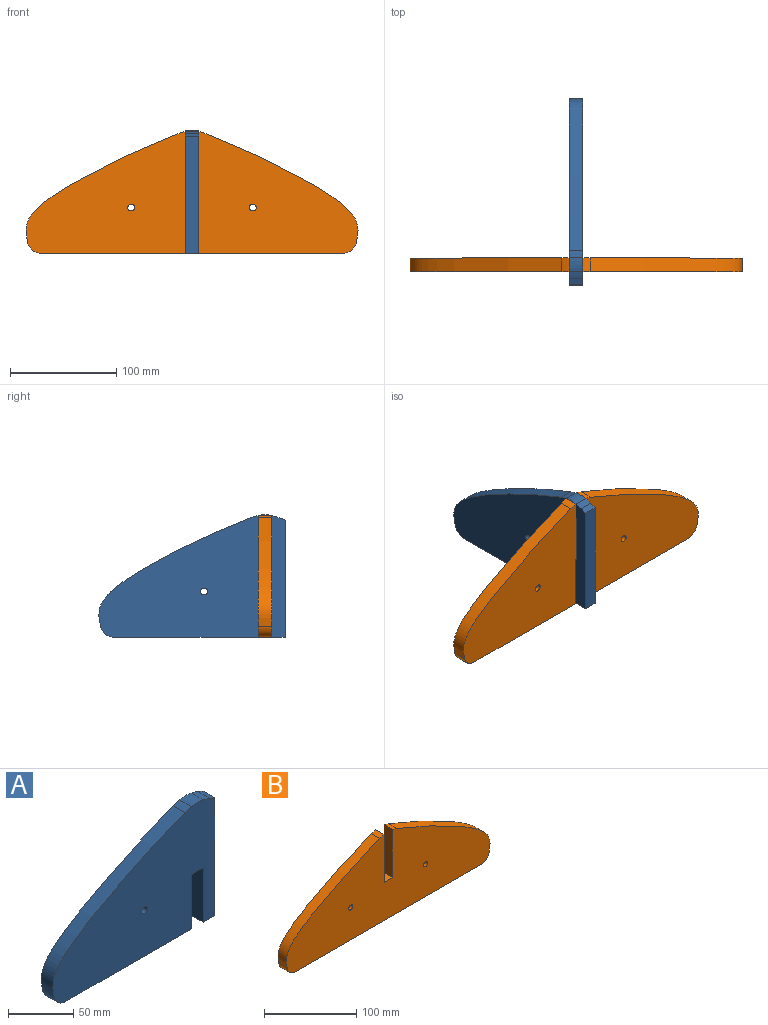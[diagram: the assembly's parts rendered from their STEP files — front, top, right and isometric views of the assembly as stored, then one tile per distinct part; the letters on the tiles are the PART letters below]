
ASSEMBLY  parts=2 mates=1
PART A: 15 faces, bbox 178.9x12.7x115.2 mm
  f0: extruded ~142.72x102mm, area 2355.1mm2, adj f1,f12,f13,f14
  f1: cylinder r=12.7mm len=12.7mm, axis (0,1,0), area 222.9mm2, adj f0,f2,f13,f14
  f2: plane 135.65x12.7mm, normal (0,0,-1), area 1722.8mm2, adj f1,f3,f13,f14
  f3: plane 50.8x12.7mm, normal (1,0,0), area 645.2mm2, adj f2,f4,f13,f14
  f4: plane 12.7x12.63mm, normal (0,0,-1), area 160.4mm2, adj f3,f5,f13,f14
  f5: plane 50.8x12.7mm, normal (-1,0,0), area 645.2mm2, adj f4,f6,f13,f14
  f6: plane 12.7x12.7mm, normal (0,0,-1), area 161.3mm2, adj f5,f7,f13,f14
  f7: plane 110.07x12.7mm, normal (1,0,0), area 1397.9mm2, adj f6,f8,f13,f14
  f8: extruded ~12.7x5.72mm, area 78mm2, adj f7,f9,f13,f14
  f9: cylinder r=50.8mm len=12.7mm, axis (0,1,0), area 91.9mm2, adj f8,f10,f13,f14
  f10: cylinder r=28.26mm len=12.7mm, axis (0,1,0), area 162.7mm2, adj f9,f12,f13,f14
  f11: cylinder r=3.17mm len=12.7mm, axis (0,1,0), area 253.4mm2, adj f13,f14
  f12: cylinder r=50.8mm len=12.7mm, axis (0,1,0), area 91.9mm2, adj f0,f10,f13,f14
  f13: plane 178.95x115.16mm, normal (0,-1,0), area 14079.7mm2, adj f0,f1,f2,f3,f4,f5,f6,f7
  f14: plane 178.95x115.16mm, normal (0,1,0), area 14079.7mm2, adj f0,f1,f2,f3,f4,f5,f6,f7
PART B: 14 faces, bbox 319.9x12.7x114.4 mm
  f0: plane 63.64x12.7mm, normal (1,0,0), area 808.2mm2, adj f1,f11,f12,f13
  f1: cylinder r=50.8mm len=12.7mm, axis (0,1,0), area 91.9mm2, adj f0,f2,f12,f13
  f2: extruded ~142.72x102mm, area 2355.1mm2, adj f1,f3,f12,f13
  f3: cylinder r=12.7mm len=12.7mm, axis (0,1,0), area 222.9mm2, adj f2,f4,f12,f13
  f4: plane 284x12.7mm, normal (0,0,-1), area 3606.8mm2, adj f3,f5,f12,f13
  f5: cylinder r=12.7mm len=12.7mm, axis (0,1,0), area 222.9mm2, adj f4,f6,f12,f13
  f6: extruded ~142.72x102mm, area 2355.1mm2, adj f5,f7,f12,f13
  f7: cylinder r=50.8mm len=12.7mm, axis (0,1,0), area 91.9mm2, adj f6,f8,f12,f13
  f8: plane 63.64x12.7mm, normal (-1,0,0), area 808.2mm2, adj f7,f11,f12,f13
  f9: cylinder r=3.17mm len=12.7mm, axis (0,1,0), area 253.4mm2, adj f12,f13
  f10: cylinder r=3.17mm len=12.7mm, axis (0,1,0), area 253.4mm2, adj f12,f13
  f11: plane 12.7x12.7mm, normal (0,0,1), area 161.3mm2, adj f0,f8,f12,f13
  f12: plane 319.94x114.44mm, normal (0,-1,0), area 24327.6mm2, adj f0,f1,f2,f3,f4,f5,f6,f7
  f13: plane 319.94x114.44mm, normal (0,1,0), area 24327.6mm2, adj f0,f1,f2,f3,f4,f5,f6,f7
PLACE A rot(axis=(0,0,-1),90deg) t=(5.5,-0.04,19.67)mm
PLACE B t=(93.78,6.35,-34.71)mm
MATE fastened A.f4 <-> B.f11  axis (0,0,-1) through (-0.85,0,16.09)mm
